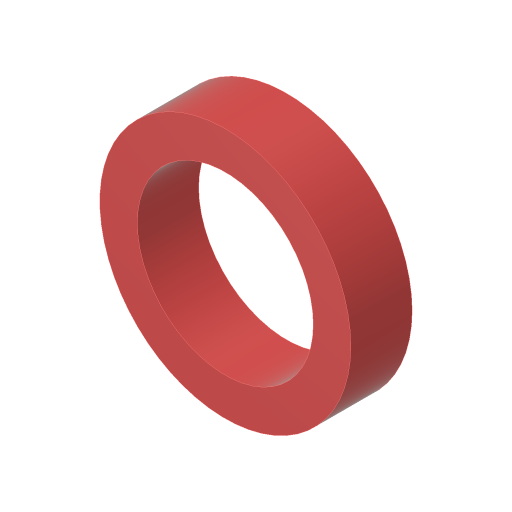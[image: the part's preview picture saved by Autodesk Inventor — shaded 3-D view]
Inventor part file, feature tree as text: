
AUTODESK INVENTOR PART (.ipt)
format: ipt  version: 2023.4 (Build 274418000, 418)  size: 114,688 bytes
history: native  units: in
note: dims shown in document units (in); Inventor stores cm internally (conversion verified against a paired STEP export)
features: extrude x1, sketch x1
ambient origin geometry x8: Origin, YZ Plane, XZ Plane, XY Plane, X Axis, Y Axis, Z Axis, Center Point
bodies: Solid1 (feature_tree)
feature tree (2):
  extrude  "Extrusion1"  Depth=0.204in
  sketch  "Sketch1"  dims[d0=0.585in d1=0.125in d2=0.204in d3=0.0in]
